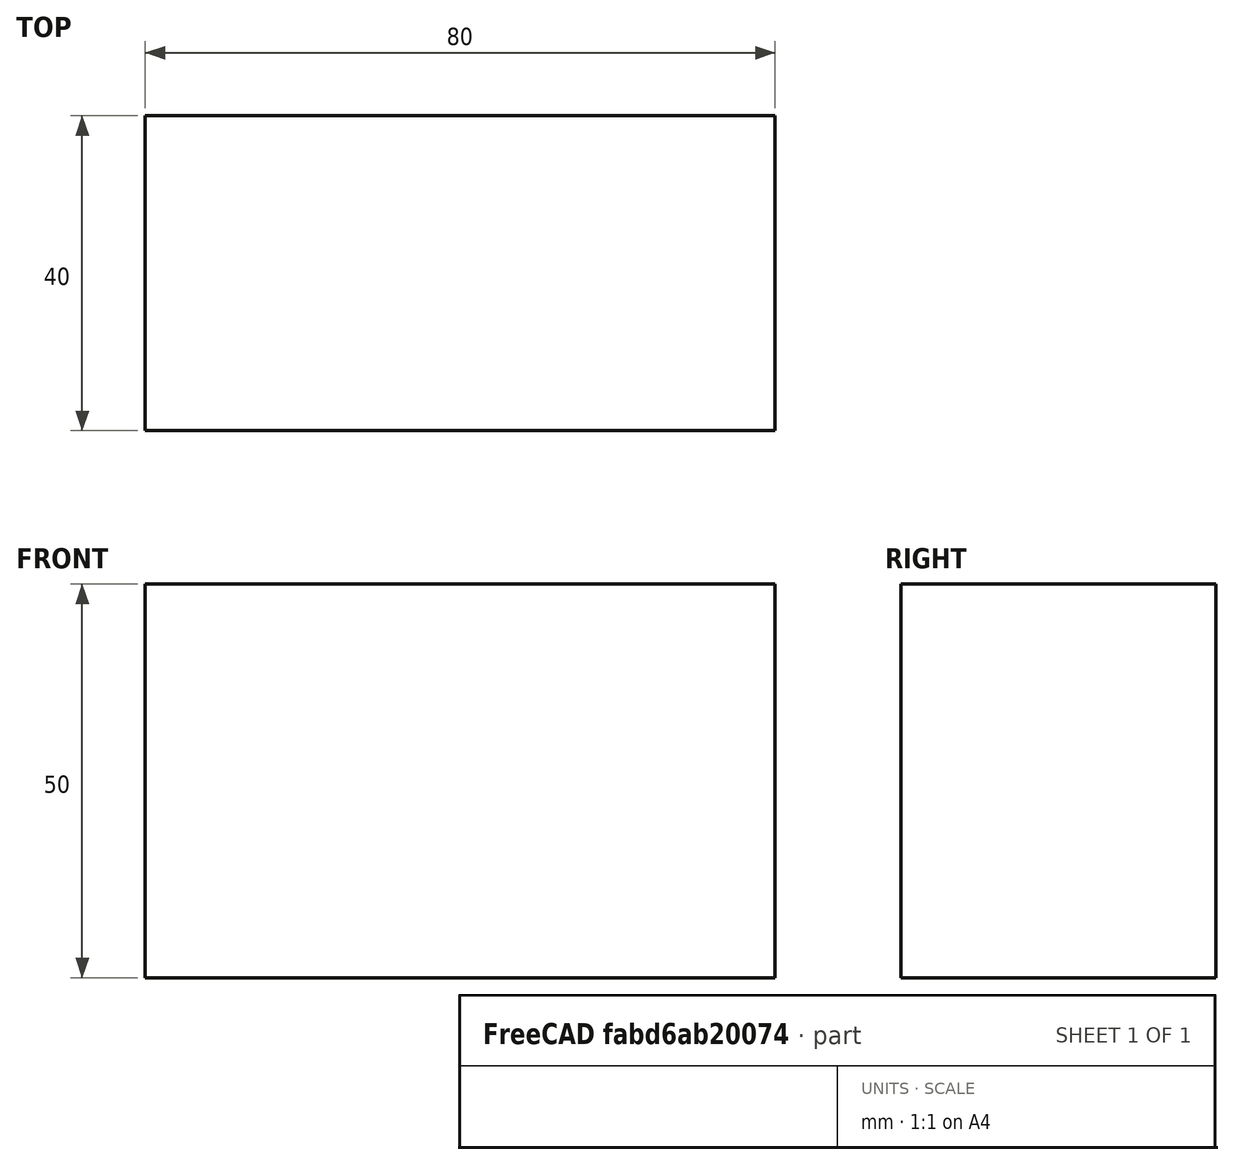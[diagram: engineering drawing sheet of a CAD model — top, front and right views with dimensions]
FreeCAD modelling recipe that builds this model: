
FCSTD DOCUMENT  (FreeCAD 0.15R4671 (Git))
Label: Flat Bar 80x40 EN10058 S235JR
License: All rights reserved
LicenseURL: http://en.wikipedia.org/wiki/All_rights_reserved
objects: Sketcher::SketchObject×1, Part::Extrusion×1
note: 2 computed .brp shape members not serialized (recipe doc carries the construction recipe); baked Part::Feature solids carry a one-line shape summary decoded from their .brp

FEATURE [Sketcher::SketchObject] Sketch
  sketch-geometry (4):
    g0: LineSegment StartX=-40 StartY=-20 StartZ=0 EndX=40 EndY=-20 EndZ=0
    g1: LineSegment StartX=40 StartY=-20 StartZ=0 EndX=40 EndY=20 EndZ=0
    g2: LineSegment StartX=40 StartY=20 StartZ=0 EndX=-40 EndY=20 EndZ=0
    g3: LineSegment StartX=-40 StartY=20 StartZ=0 EndX=-40 EndY=-20 EndZ=0
  constraints (12):
    c: Coincident(g0,g1)
    c: Coincident(g1,g2)
    c: Coincident(g2,g3)
    c: Coincident(g3,g0)
    c: Horizontal(g0)
    c: Horizontal(g2)
    c: Vertical(g1)
    c: Vertical(g3)
    c: Symmetric(g1,g2,g-2)
    c: Symmetric(g0,g1,g-1)
    c: DistanceY(g1) = 40
    c: DistanceX(g0) = 80
FEATURE [Part::Extrusion] Extrude  label="Flat Bar 80x40 EN10058 S235JR"
  Base = -> Sketch
  Dir = (0,0,50)
  Solid = true
